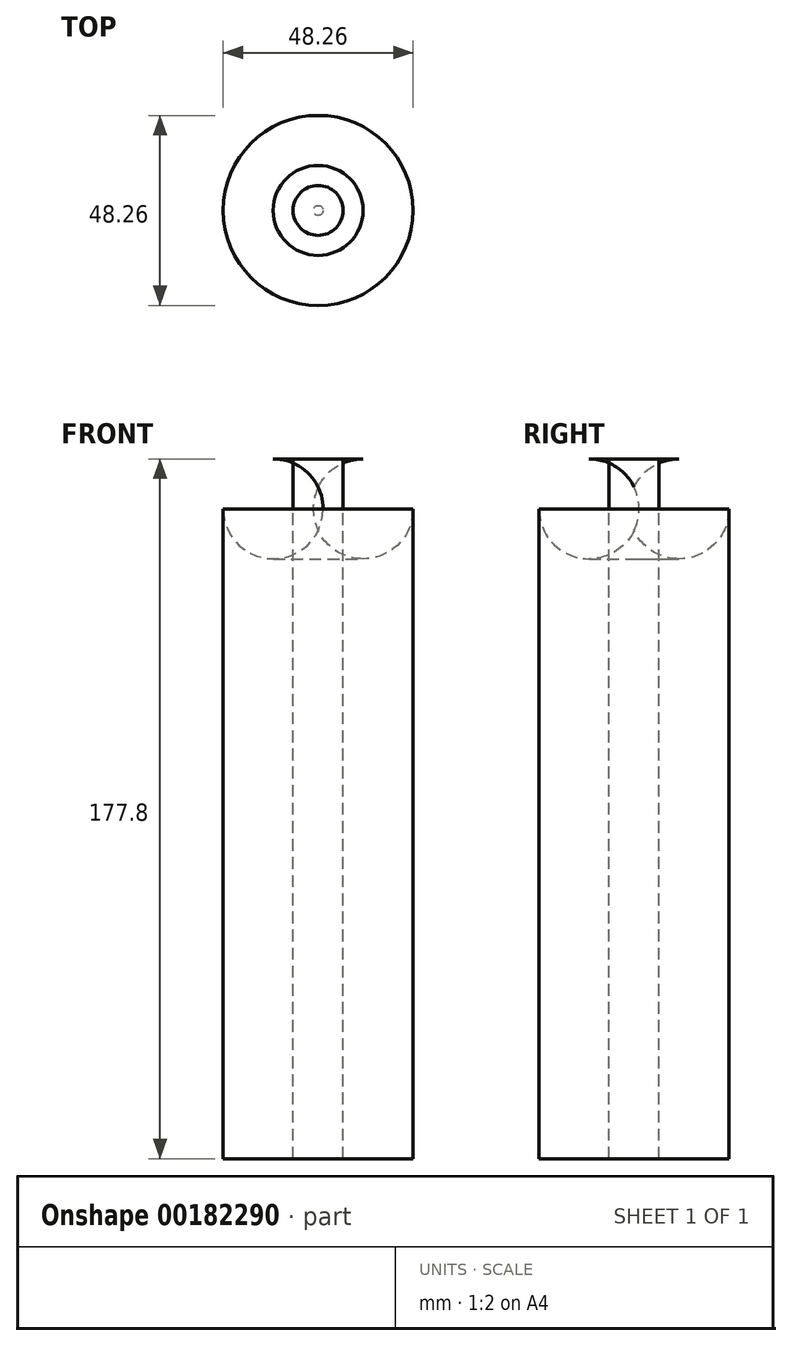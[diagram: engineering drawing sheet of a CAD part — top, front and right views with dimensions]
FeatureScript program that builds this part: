
annotation { "Feature Type Name" : "Feature", "Feature Type Description" : "" }
export const myFeature = defineFeature(function(context is Context, id is Id, definition is map)
    precondition{}
    {
        {
            var Q0;
            Q0=qCreatedBy(makeId("Front.planeOp"),FACE);
            var sketch = newSketch(context, id + "F0", { "sketchPlane" : qUnion([Q0])});
            skLineSegment(sketch, "E0.bottom", {"start": v(0, 0) * mm, "end": v(24.13, 0) * mm});
            skLineSegment(sketch, "E0.top", {"start": v(0, 177.8) * mm, "end": v(11.43, 177.8) * mm});
            skLineSegment(sketch, "E0.left", {"start": v(0, 0) * mm, "end": v(0, 177.8) * mm});
            skLineSegment(sketch, "E0.right", {"start": v(24.13, 0) * mm, "end": v(24.13, 165.1) * mm});
            skPoint(sketch, "E1.visualSharp", {"position": v(24.13, 177.8) * mm});
            skArc(sketch, "E1.filletArc", {"start": v(24.13, 165.1) * mm, "mid": v(20.41, 174.08) * mm, "end": v(11.43, 177.8) * mm});
            skSolve(sketch);
        }
        {
            var Q0;
            Q0 = qSketchRegion(id + "F0", true);
            var Q1;
            Q1=sQuery(id+"F0.wireOp",EDGE,"E0.left");
            revolve(context, id + "F1", {"entities" : qUnion([Q0]), "axis" : qUnion([Q1]), "revolveType" : RevolveType.FULL});
        }
        {
            var Q0;
            Q0=makeQuery(id+"F1.opRevolve","SWEPT_FACE",FACE,{"disambiguationData":[OSD([sQuery(id+"F0.wireOp",EDGE,"E0.top")])]});
            var sketch = newSketch(context, id + "F2", { "sketchPlane" : qUnion([Q0])});
            skCircle(sketch, "E2", {"center": v(0, 0) * mm, "radius": 6.35 * mm});
            skSolve(sketch);
        }
        {
            var Q0;
            Q0 = qSketchRegion(id + "F2", true);
            extrude(context, id + "F3", {"entities" : qUnion([Q0]), "operationType" : NewBodyOperationType.REMOVE, "oppositeDirection" : true, "depth" : 177.8 * mm});
        }
    });
